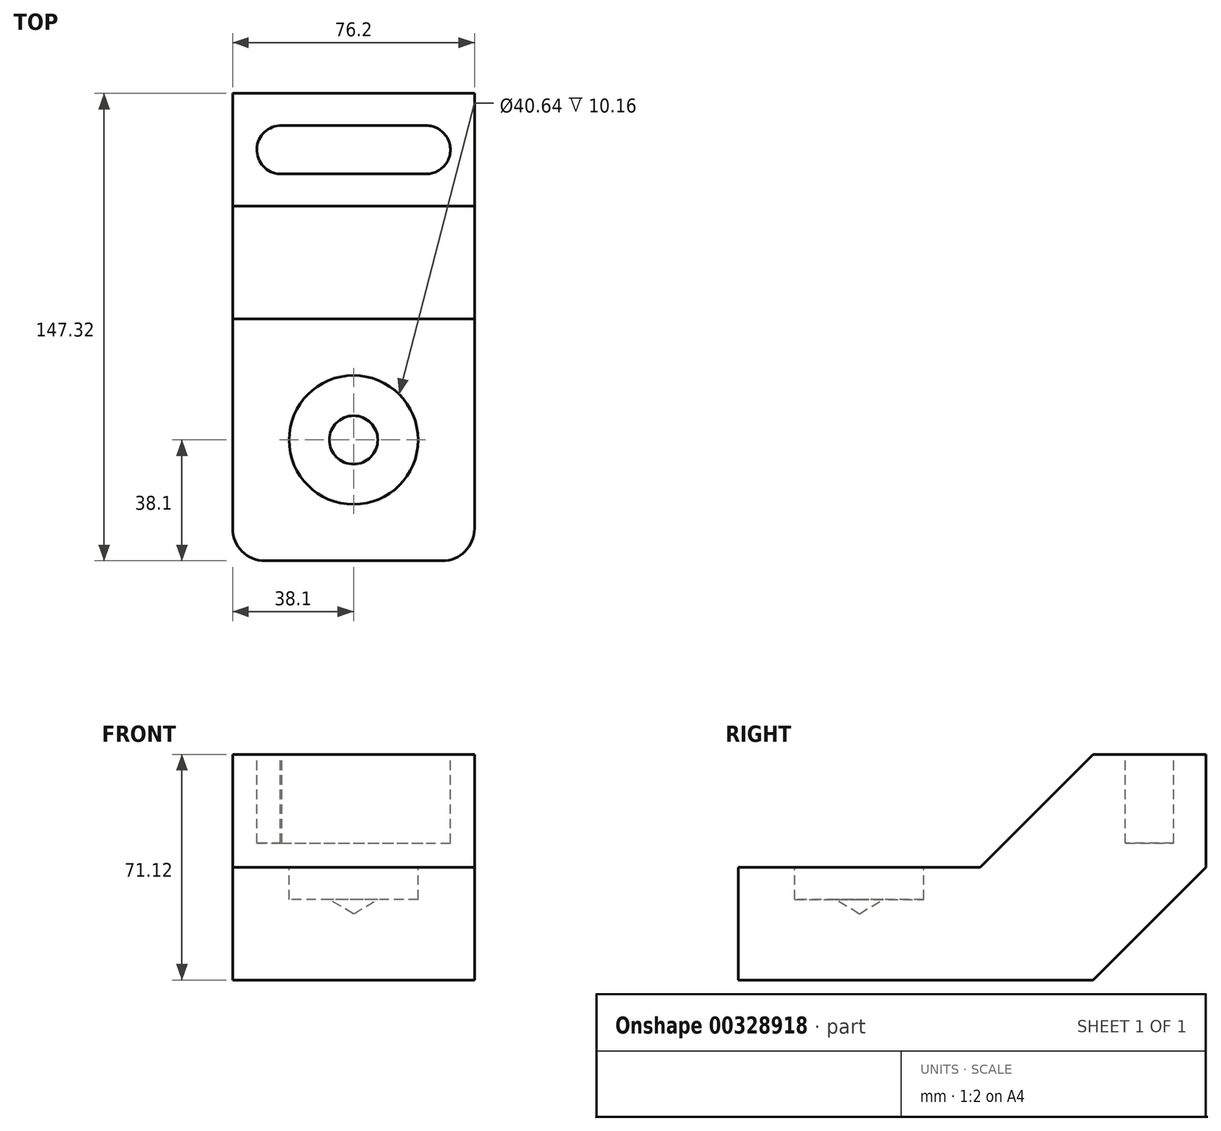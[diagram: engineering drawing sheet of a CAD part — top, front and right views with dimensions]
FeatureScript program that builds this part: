
annotation { "Feature Type Name" : "Feature", "Feature Type Description" : "" }
export const myFeature = defineFeature(function(context is Context, id is Id, definition is map)
    precondition{}
    {
        {
            var Q0;
            Q0=qCreatedBy(makeId("Right.planeOp"),FACE);
            var sketch = newSketch(context, id + "F0", { "sketchPlane" : qUnion([Q0])});
            skLineSegment(sketch, "E0.bottom", {"start": v(0, 0) * mm, "end": v(35.56, 0) * mm});
            skLineSegment(sketch, "E0.top", {"start": v(35.56, 71.12) * mm, "end": v(71.12, 71.12) * mm});
            skLineSegment(sketch, "E0.left", {"start": v(0, 0) * mm, "end": v(0, 35.56) * mm});
            skLineSegment(sketch, "E0.right", {"start": v(71.12, 35.56) * mm, "end": v(71.12, 71.12) * mm});
            skPoint(sketch, "E1", {"position": v(35.56, 0) * mm});
            skPoint(sketch, "E2", {"position": v(71.12, 35.56) * mm});
            skLineSegment(sketch, "E3", {"start": v(71.12, 35.56) * mm, "end": v(35.56, 0) * mm});
            skPoint(sketch, "E4", {"position": v(35.56, 71.12) * mm});
            skPoint(sketch, "E5", {"position": v(0, 35.56) * mm});
            skLineSegment(sketch, "E6", {"start": v(35.56, 71.12) * mm, "end": v(0, 35.56) * mm});
            skPoint(sketch, "E7.orphan", {"position": v(71.12, 0) * mm});
            skSolve(sketch);
        }
        {
            var Q0;
            Q0 = qSketchRegion(id + "F0", true);
            extrude(context, id + "F1", {"entities" : qUnion([Q0]), "depth" : 76.2 * mm});
        }
        {
            var Q0;
            Q0=makeQuery(id+"F1.opExtrude","SWEPT_FACE",FACE,{"disambiguationData":[OSD([sQuery(id+"F0.wireOp",EDGE,"E0.left")])]});
            extrude(context, id + "F2", {"entities" : qUnion([Q0]), "operationType" : NewBodyOperationType.ADD, "depth" : 76.2 * mm});
        }
        {
            var Q0;
            Q0=makeQuery(id+"F2.opExtrude","SWEPT_FACE",FACE,{"disambiguationData":[OSD([sQuery(id+"F0.wireOp",EDGE,"E0.left"),sQuery(id+"F0.wireOp",EDGE,"E6")])]});
            var sketch = newSketch(context, id + "F3", { "sketchPlane" : qUnion([Q0])});
            skPoint(sketch, "E8", {"position": v(38.1, -38.1) * mm});
            skPoint(sketch, "E8.positionSnap0", {"position": v(38.1, -76.2) * mm});
            skSolve(sketch);
        }
        {
            var Q0;
            Q0=sQuery(id+"F3.wireOp",VERTEX,"E8");
            var Q1;
            Q1=makeQuery(id+"F1.opExtrude","SWEPT_BODY",BODY,{"disambiguationData":[OSD([sQuery(id+"F0.wireOp",EDGE,"E0.bottom"),sQuery(id+"F0.wireOp",EDGE,"E0.top"),sQuery(id+"F0.wireOp",EDGE,"E0.left"),sQuery(id+"F0.wireOp",EDGE,"E0.right"),sQuery(id+"F0.wireOp",EDGE,"E3"),sQuery(id+"F0.wireOp",EDGE,"E6")])]});
            hole(context, id + "F4", {"style" : HoleStyle.C_BORE, "endStyle" : HoleEndStyle.BLIND, "holeDiameter" : 15.24 * mm, "cBoreDiameter" : 40.64 * mm, "cBoreDepth" : 10.16 * mm, "holeDepth" : 10.16 * mm, "tappedDepth" : 12.7 * mm, "tapClearance" : 3, "locations" : qUnion([Q0]), "scope" : qUnion([Q1])});
        }
        {
            var Q0;
            {var subQ0=sQuery(id+"F0.wireOp",EDGE,"E0.left");Q0=makeQuery(id+"F2.opExtrude","CAP_EDGE",EDGE,{"disambiguationData":[OSD([subQ0]),TDD([makeQuery(id+"F1.opExtrude","CAP_EDGE",EDGE,{"disambiguationData":[OSD([subQ0])],"isStart":false})])],"isStart":false});}
            fillet(context, id + "F5", {"entities" : qUnion([Q0]), "radius" : 10.16 * mm, "tangentPropagation" : true, "allowEdgeOverflow" : false});
        }
        {
            var Q0;
            {var subQ0=sQuery(id+"F0.wireOp",EDGE,"E0.left");Q0=makeQuery(id+"F2.opExtrude","CAP_EDGE",EDGE,{"disambiguationData":[OSD([subQ0]),TDD([makeQuery(id+"F1.opExtrude","CAP_EDGE",EDGE,{"disambiguationData":[OSD([subQ0])],"isStart":true})])],"isStart":false});}
            fillet(context, id + "F6", {"entities" : qUnion([Q0]), "radius" : 10.16 * mm, "tangentPropagation" : true, "allowEdgeOverflow" : false});
        }
        {
            var Q0;
            Q0=makeQuery(id+"F1.opExtrude","SWEPT_FACE",FACE,{"disambiguationData":[OSD([sQuery(id+"F0.wireOp",EDGE,"E0.top")])]});
            var sketch = newSketch(context, id + "F7", { "sketchPlane" : qUnion([Q0])});
            skPoint(sketch, "E9.positionSnap0", {"position": v(0, 53.34) * mm});
            skPoint(sketch, "E10.positionSnap0", {"position": v(76.2, 53.34) * mm});
            skArc(sketch, "E11", {"start": v(15.52, 60.95) * mm, "mid": v(7.62, 53.34) * mm, "end": v(15.52, 45.73) * mm});
            skArc(sketch, "E12", {"start": v(60.96, 45.72) * mm, "mid": v(68.58, 53.34) * mm, "end": v(60.96, 60.96) * mm});
            skLineSegment(sketch, "E13", {"start": v(15.52, 60.95) * mm, "end": v(60.96, 60.96) * mm});
            skLineSegment(sketch, "E14", {"start": v(14.96, 45.73) * mm, "end": v(60.96, 45.72) * mm});
            skSolve(sketch);
        }
        {
            var Q0;
            {var subQ5=sQuery(id+"F7.wireOp",EDGE,"E12");Q0=makeQuery(id+"F7.imprint","IMPRINT",FACE,{"disambiguationData":[TD([[makeQuery(id+"F7.imprint","IMPRINT",EDGE,{"derivedFrom":subQ5}),1.0]])]});}
            extrude(context, id + "F8", {"entities" : qUnion([Q0]), "operationType" : NewBodyOperationType.REMOVE, "oppositeDirection" : true, "depth" : 27.94 * mm});
        }
    });
